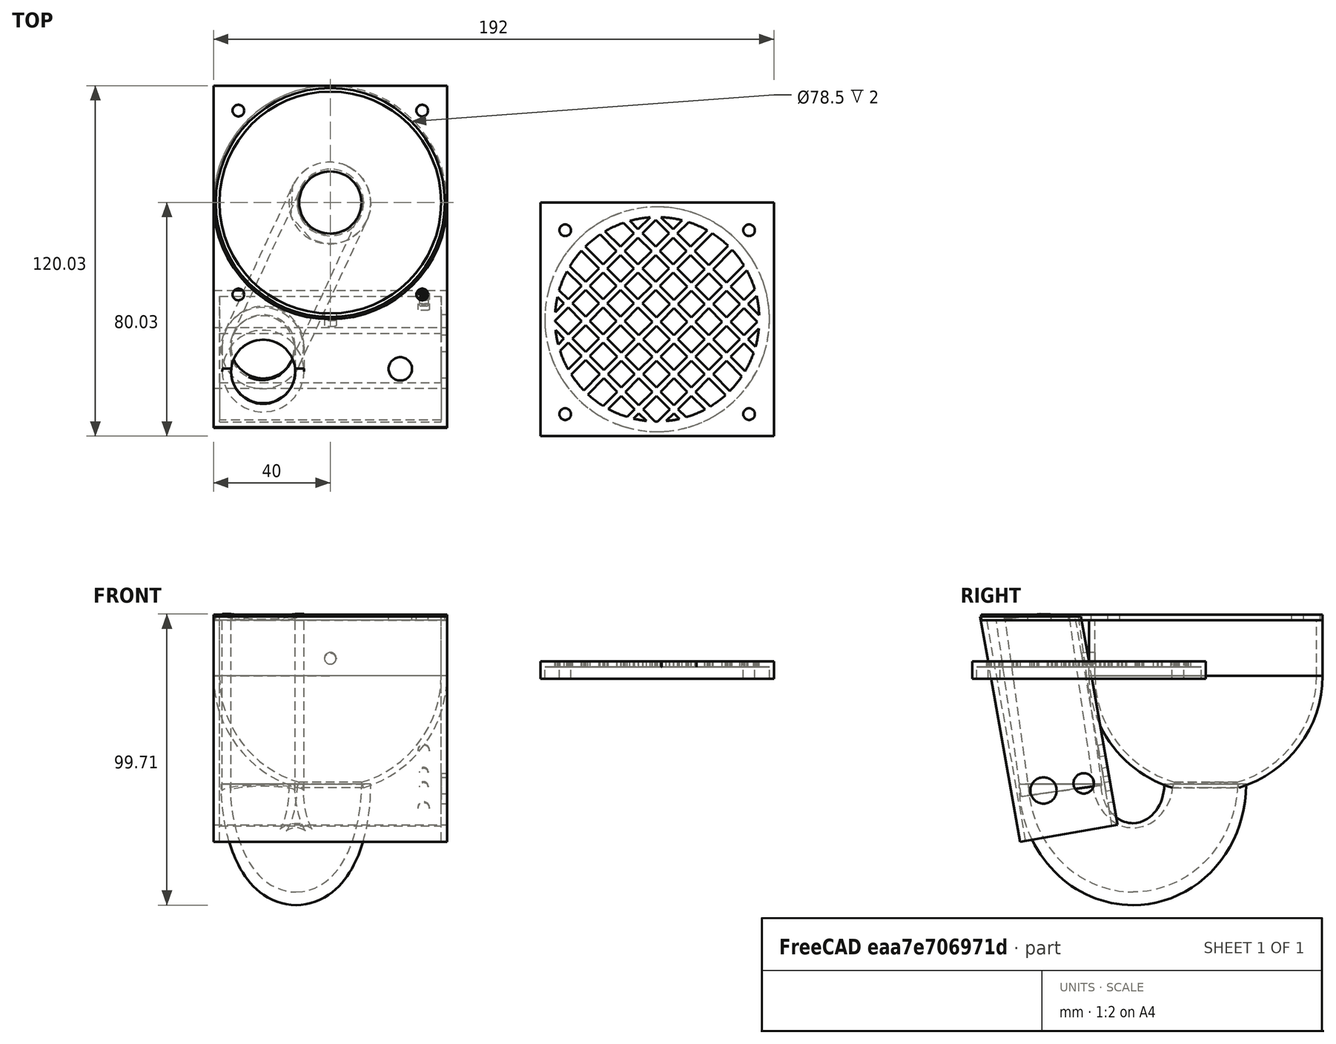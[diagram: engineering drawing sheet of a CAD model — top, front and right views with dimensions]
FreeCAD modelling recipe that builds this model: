
FCSTD DOCUMENT  (FreeCAD 0.18R16146 (Git))
Label: 10W75mmCabinet
License: All rights reserved
LicenseURL: http://en.wikipedia.org/wiki/All_rights_reserved
objects: Part::Cylinder×27, Part::Box×21, Part::MultiFuse×10, Part::Cut×7, Part::Sphere×3, Sketcher::SketchObject×2, Part::Sweep×2, Part::Spiral×1, PartDesign::Body×1
note: 74 computed .brp shape members not serialized (recipe doc carries the construction recipe); baked Part::Feature solids carry a one-line shape summary decoded from their .brp

FEATURE [Part::Sphere] Sphere  label="DomePunch"
  Angle1 = -90
  Angle2 = 90
  Angle3 = 360
  AttacherType = Attacher::AttachEngine3D
  Placement = pos=(38,38,0) rot=(0,0,1;0rad)
  Radius = 38
FEATURE [Part::Sphere] Sphere001  label="Dome"
  Angle1 = -90
  Angle2 = 90
  Angle3 = 360
  AttacherType = Attacher::AttachEngine3D
  Placement = pos=(38,38,0) rot=(0,0,1;0rad)
  Radius = 40
FEATURE [Part::Box] Box001  label="DomeSlice"
  AttacherType = Attacher::AttachEngine3D
  Height = 40
  Length = 80
  Placement = pos=(-2,-2,0) rot=(0,0,1;0rad)
  Width = 80
FEATURE [Part::Cylinder] Cylinder  label="DepthPunch"
  Angle = 360
  AttacherType = Attacher::AttachEngine3D
  Height = 20
  Placement = pos=(38,38,-1) rot=(0,0,1;0rad)
  Radius = 38
FEATURE [Part::Cylinder] Cylinder001  label="Depth"
  Angle = 360
  AttacherType = Attacher::AttachEngine3D
  Height = 19
  Placement = pos=(38,38,-1) rot=(0,0,1;0rad)
  Radius = 40
FEATURE [Part::Box] Box002  label="Mount"
  AttacherType = Attacher::AttachEngine3D
  Height = 2
  Length = 80
  Placement = pos=(-2,-39,20) rot=(0,0,1;0rad)
  Width = 117
FEATURE [Part::Cylinder] Cylinder002  label="MountPunch"
  Angle = 360
  AttacherType = Attacher::AttachEngine3D
  Height = 2
  Placement = pos=(38,38,20) rot=(0,0,1;0rad)
  Radius = 39.25
FEATURE [Part::Cylinder] Cylinder003  label="MountHole"
  Angle = 360
  AttacherType = Attacher::AttachEngine3D
  Height = 2
  Placement = pos=(0,0,20) rot=(0,0,1;0rad)
  Radius = 2
FEATURE [Part::Cylinder] Cylinder004  label="MountHole001"
  Angle = 360
  AttacherType = Attacher::AttachEngine3D
  Height = 2
  Placement = pos=(63,0,20) rot=(0,0,1;0rad)
  Radius = 2
FEATURE [Part::Cylinder] Cylinder005  label="MountHole002"
  Angle = 360
  AttacherType = Attacher::AttachEngine3D
  Height = 2
  Placement = pos=(63,63,20) rot=(0,0,1;0rad)
  Radius = 2
FEATURE [Part::Cylinder] Cylinder006  label="MountHole003"
  Angle = 360
  AttacherType = Attacher::AttachEngine3D
  Height = 2
  Placement = pos=(0,63,20) rot=(0,0,1;0rad)
  Radius = 2
FEATURE [Part::MultiFuse] Fusion  label="MountHoles"
  Placement = pos=(6.5,6.5,0) rot=(0,0,1;0rad)
  Shapes = -> [Cylinder003,Cylinder005,Cylinder006,Cylinder004]
FEATURE [Part::Box] Box003  label="Base"
  AttacherType = Attacher::AttachEngine3D
  Height = 80
  Length = 80
  Placement = pos=(-2,-33,-51) rot=(0,0,1;0rad)
  Width = 34
FEATURE [Part::Box] Box004  label="BasePunch"
  AttacherType = Attacher::AttachEngine3D
  Height = 78
  Length = 76
  Placement = pos=(0,-31,-51) rot=(0,0,1;0rad)
  Width = 30
FEATURE [Part::Cylinder] Cylinder007  label="BaseHole"
  Angle = 360
  AttacherType = Attacher::AttachEngine3D
  Height = 2
  Placement = pos=(15,-19,20) rot=(0,0,1;0rad)
  Radius = 11
FEATURE [Part::Sphere] Sphere002  label="DomeHole"
  Angle1 = -90
  Angle2 = 90
  Angle3 = 360
  AttacherType = Attacher::AttachEngine3D
  Placement = pos=(38,38,-42) rot=(0,0,1;0rad)
  Radius = 12
FEATURE [Part::MultiFuse] Fusion003  label="DOMEPUNCH"
  Shapes = -> [Sphere002,Sphere,Box001]
FEATURE [Part::Cut] Cut  label="DOME"
  Base = -> Sphere001
  Placement = pos=(0,2,1) rot=(0,0,1;0rad)
  Tool = -> Fusion003
FEATURE [Part::Cylinder] Cylinder008  label="Tube"
  Angle = 360
  AttacherType = Attacher::AttachEngine3D
  Height = 61
  Placement = pos=(15,-20,-39) rot=(0,0,1;0rad)
  Radius = 14
FEATURE [Part::Cylinder] Cylinder009  label="TubePunch"
  Angle = 360
  AttacherType = Attacher::AttachEngine3D
  Height = 61
  Placement = pos=(15,-20,-39) rot=(0,0,1;0rad)
  Radius = 11
FEATURE [Part::Spiral] Spiral001  label="TubeSpiral"
  AttacherType = Attacher::AttachEngine3D
  Growth = 1
  Placement = pos=(-2e-16,23,-70) rot=(0,0,1;1.5708rad)
  Radius = 27
  Rotations = 0.5
FEATURE [Part::Cylinder] Cylinder010  label="WireHole"
  Angle = 360
  AttacherType = Attacher::AttachEngine3D
  Height = 3
  Placement = pos=(38,1,5) rot=(1,0,0;1.5708rad)
  Radius = 2
FEATURE [Part::MultiFuse] Fusion004  label="DEPTHPUNCH"
  Shapes = -> [Cylinder,Cylinder010]
FEATURE [Part::Cut] Cut007  label="DEPTH"
  Base = -> Cylinder001
  Placement = pos=(0,2,2) rot=(0,0,1;0rad)
  Tool = -> Fusion004
FEATURE [Part::Cylinder] Cylinder012  label="VolumeHole"
  Angle = 360
  AttacherType = Attacher::AttachEngine3D
  Height = 2
  Placement = pos=(62,-20,20) rot=(0,0,1;0rad)
  Radius = 2.5
FEATURE [Part::Cylinder] Cylinder013  label="ExtSpeakerHole"
  Angle = 360
  AttacherType = Attacher::AttachEngine3D
  Height = 2
  Placement = pos=(70,1,-45) rot=(1,0,0;1.5708rad)
  Radius = 2
FEATURE [Part::Cylinder] Cylinder014  label="AudioInHole"
  Angle = 360
  AttacherType = Attacher::AttachEngine3D
  Height = 2
  Placement = pos=(76,-8,-35) rot=(0,1,0;1.5708rad)
  Radius = 3.5
FEATURE [Part::Cylinder] Cylinder015  label="PowerInHole"
  Angle = 360
  AttacherType = Attacher::AttachEngine3D
  Height = 2
  Placement = pos=(76,-22,-35) rot=(0,1,0;1.5708rad)
  Radius = 4.5
FEATURE [Sketcher::SketchObject] Sketch001  label="TubeSketchOuter"
  MapMode = 5
  Placement = pos=(0,0,0) rot=(0.57735,0.57735,0.57735;2.0944rad)
  Support = -> [YZ_Plane]
  sketch-geometry (1):
    g0: Circle CenterX=50.1616 CenterY=-70.1288 CenterZ=0 NormalX=0 NormalY=0 NormalZ=1 AngleXU=0 Radius=14.0264
FEATURE [Part::Sweep] Sweep
  Frenet = false
  Placement = pos=(-45.2015,16.8804,-37.1345) rot=(-0.179283,-0.967324,-0.179283;1.60401rad)
  Sections = -> [Sketch001]
  Solid = true
  Spine = -> Spiral001 [Edge1]
  Transition = 1
FEATURE [Sketcher::SketchObject] Sketch  label="SketchInner"
  MapMode = 5
  Placement = pos=(0,0,0) rot=(0.57735,0.57735,0.57735;2.0944rad)
  Support = -> [YZ_Plane]
  sketch-geometry (1):
    g0: Circle CenterX=50.2486 CenterY=-70.2529 CenterZ=0 NormalX=0 NormalY=0 NormalZ=1 AngleXU=0 Radius=11.0039
FEATURE [PartDesign::Body] Body  label="TubeBodyOuter"
  Group = -> [Sketch001,Sketch]
  Origin = -> Origin
FEATURE [Part::Sweep] Sweep001
  Frenet = false
  Placement = pos=(-45.3803,16.9935,-35.5882) rot=(-0.179283,-0.967324,-0.179283;1.60401rad)
  Sections = -> [Sketch]
  Solid = true
  Spine = -> Spiral001 [Edge1]
  Transition = 1
FEATURE [Part::Cut] Cut008  label="TUBE_CURVE"
  Base = -> Sweep
  Placement = pos=(-3,4,1) rot=(0,0,-1;0.069813rad)
  Tool = -> Sweep001
FEATURE [Part::Cylinder] Cylinder016  label="FaceHole"
  Angle = 360
  AttacherType = Attacher::AttachEngine3D
  Height = 4
  Placement = pos=(150,0,0) rot=(0,0,1;0rad)
  Radius = 38.5
FEATURE [Part::Box] Box  label="Face"
  AttacherType = Attacher::AttachEngine3D
  Height = 6
  Length = 80
  Placement = pos=(110,-40,0) rot=(0,0,1;0rad)
  Width = 80
FEATURE [Part::Cylinder] Cylinder017  label="FaceSpace"
  Angle = 360
  AttacherType = Attacher::AttachEngine3D
  Height = 2
  Placement = pos=(150,0,4) rot=(0,0,1;0rad)
  Radius = 35
FEATURE [Part::Cylinder] Cylinder018  label="MountHole004"
  Angle = 360
  AttacherType = Attacher::AttachEngine3D
  Height = 6
  Placement = pos=(0,0,20) rot=(0,0,1;0rad)
  Radius = 2
FEATURE [Part::Cylinder] Cylinder019  label="MountHole005"
  Angle = 360
  AttacherType = Attacher::AttachEngine3D
  Height = 6
  Placement = pos=(63,0,20) rot=(0,0,1;0rad)
  Radius = 2
FEATURE [Part::Cylinder] Cylinder020  label="MountHole006"
  Angle = 360
  AttacherType = Attacher::AttachEngine3D
  Height = 6
  Placement = pos=(63,63,20) rot=(0,0,1;0rad)
  Radius = 2
FEATURE [Part::Cylinder] Cylinder021  label="MountHole007"
  Angle = 360
  AttacherType = Attacher::AttachEngine3D
  Height = 6
  Placement = pos=(0,63,20) rot=(0,0,1;0rad)
  Radius = 2
FEATURE [Part::MultiFuse] Fusion006  label="FaceMountHoles"
  Placement = pos=(118.5,-32.5,-20) rot=(0,0,1;0rad)
  Shapes = -> [Cylinder018,Cylinder020,Cylinder021,Cylinder019]
FEATURE [Part::MultiFuse] Fusion005  label="FacePunch"
  Shapes = -> [Cylinder017,Cylinder016,Fusion006]
FEATURE [Part::Box] Box005  label="Grill"
  AttacherType = Attacher::AttachEngine3D
  Height = 2
  Length = 75
  Placement = pos=(124.5,-27.5,4) rot=(0,0,1;0.785398rad)
  Width = 2
FEATURE [Part::Box] Box006  label="Grill001"
  AttacherType = Attacher::AttachEngine3D
  Height = 2
  Length = 75
  Placement = pos=(122.5,25,4) rot=(0,0,-1;0.785398rad)
  Width = 2
FEATURE [Part::Box] Box007  label="Grill002"
  AttacherType = Attacher::AttachEngine3D
  Height = 2
  Length = 75
  Placement = pos=(118,-21.5,4) rot=(0,0,1;0.785398rad)
  Width = 2
FEATURE [Part::Box] Box008  label="Grill003"
  AttacherType = Attacher::AttachEngine3D
  Height = 2
  Length = 58
  Placement = pos=(112,-3.5,4) rot=(0,0,1;0.785398rad)
  Width = 2
FEATURE [Part::Box] Box009  label="Grill004"
  AttacherType = Attacher::AttachEngine3D
  Height = 2
  Length = 75
  Placement = pos=(112,-15.5,4) rot=(0,0,1;0.785398rad)
  Width = 2
FEATURE [Part::Box] Box010  label="Grill005"
  AttacherType = Attacher::AttachEngine3D
  Height = 2
  Length = 75
  Placement = pos=(128.5,31,4) rot=(0,0,-1;0.785398rad)
  Width = 2
FEATURE [Part::Box] Box011  label="Grill006"
  AttacherType = Attacher::AttachEngine3D
  Height = 2
  Length = 75
  Placement = pos=(134.5,37,4) rot=(0,0,-1;0.785398rad)
  Width = 2
FEATURE [Part::Box] Box012  label="Grill007"
  AttacherType = Attacher::AttachEngine3D
  Height = 2
  Length = 58
  Placement = pos=(146.5,37,4) rot=(0,0,-1;0.785398rad)
  Width = 2
FEATURE [Part::Box] Box013  label="Grill008"
  AttacherType = Attacher::AttachEngine3D
  Height = 2
  Length = 75
  Placement = pos=(116.5,19,4) rot=(0,0,-1;0.785398rad)
  Width = 2
FEATURE [Part::Box] Box014  label="Grill009"
  AttacherType = Attacher::AttachEngine3D
  Height = 2
  Length = 75
  Placement = pos=(110.5,13,4) rot=(0,0,-1;0.785398rad)
  Width = 2
FEATURE [Part::Box] Box015  label="Grill010"
  AttacherType = Attacher::AttachEngine3D
  Height = 2
  Length = 58
  Placement = pos=(110.5,1,4) rot=(0,0,-1;0.785398rad)
  Width = 2
FEATURE [Part::Box] Box016  label="Grill011"
  AttacherType = Attacher::AttachEngine3D
  Height = 2
  Length = 75
  Placement = pos=(130.5,-33.5,4) rot=(0,0,1;0.785398rad)
  Width = 2
FEATURE [Part::Box] Box017  label="Grill012"
  AttacherType = Attacher::AttachEngine3D
  Height = 2
  Length = 75
  Placement = pos=(136.5,-39.5,4) rot=(0,0,1;0.785398rad)
  Width = 2
FEATURE [Part::Box] Box018  label="Grill013"
  AttacherType = Attacher::AttachEngine3D
  Height = 2
  Length = 58
  Placement = pos=(148.5,-39.5,4) rot=(0,0,1;0.785398rad)
  Width = 2
FEATURE [Part::MultiFuse] Fusion007  label="GRILL"
  Shapes = -> [Box005,Box006,Box007,Box008,Box009,Box010,Box011,Box012,Box013,Box014,Box015,Box016,Box017,Box018]
FEATURE [Part::Cut] Cut009  label="FACE"
  Base = -> Box
  Tool = -> Fusion005
FEATURE [Part::Box] Box019  label="FrontLevel"
  AttacherType = Attacher::AttachEngine3D
  Height = 8
  Length = 80
  Placement = pos=(-2,-36,28) rot=(-1,0,0;0.174533rad)
  Width = 38
FEATURE [Part::Cylinder] Cylinder022  label="MountTubeHole"
  Angle = 360
  AttacherType = Attacher::AttachEngine3D
  Height = 2
  Placement = pos=(15,-20,20) rot=(0,0,1;0rad)
  Radius = 11
FEATURE [Part::Cylinder] Cylinder023  label="VolumeHole001"
  Angle = 360
  AttacherType = Attacher::AttachEngine3D
  Height = 2
  Placement = pos=(62,-19,20) rot=(0,0,1;0rad)
  Radius = 4
FEATURE [Part::MultiFuse] Fusion001  label="MOUNTPUNCH"
  Shapes = -> [Cylinder002,Fusion,Cylinder022,Cylinder023]
FEATURE [Part::Cut] Cut013  label="MOUNT"
  Base = -> Box002
  Placement = pos=(0,2,0) rot=(0,0,1;0rad)
  Tool = -> Fusion001
FEATURE [Part::Cylinder] Cylinder024  label="WireHole002"
  Angle = 360
  AttacherType = Attacher::AttachEngine3D
  Height = 3
  Placement = pos=(38,1,7) rot=(1,0,0;1.5708rad)
  Radius = 2
FEATURE [Part::Cylinder] Cylinder025  label="ExtSpeakerHole001"
  Angle = 360
  AttacherType = Attacher::AttachEngine3D
  Height = 2
  Placement = pos=(70,1,-25) rot=(1,0,0;1.5708rad)
  Radius = 2
FEATURE [Part::Cylinder] Cylinder026  label="ExtSpeakerHole002"
  Angle = 360
  AttacherType = Attacher::AttachEngine3D
  Height = 2
  Placement = pos=(70,1,-32.5) rot=(1,0,0;1.5708rad)
  Radius = 1.5
FEATURE [Part::Cylinder] Cylinder027  label="ExtSpeakerHole003"
  Angle = 360
  AttacherType = Attacher::AttachEngine3D
  Height = 2
  Placement = pos=(70,1,-37.5) rot=(1,0,0;1.5708rad)
  Radius = 1.5
FEATURE [Part::MultiFuse] Fusion008  label="BASEPUNCH"
  Shapes = -> [Box004,Cylinder007,Cylinder012,Cylinder013,Cylinder014,Cylinder015,Box019,Cylinder024,Cylinder025,Cylinder026,Cylinder027]
FEATURE [Part::Cut] Cut012  label="BASE"
  Base = -> Box003
  Placement = pos=(0,0,0) rot=(1,0,0;0.174533rad)
  Tool = -> Fusion008
FEATURE [Part::MultiFuse] Fusion009  label="FACEGRILL"
  Shapes = -> [Fusion007,Cut009]
FEATURE [Part::Box] Box020  label="FrontLevel001"
  AttacherType = Attacher::AttachEngine3D
  Height = 8
  Length = 32
  Placement = pos=(-2,-36,25) rot=(-1,0,0;0.174533rad)
  Width = 32
FEATURE [Part::MultiFuse] Fusion010  label="TUBEPUNCH"
  Shapes = -> [Box020,Cylinder009]
FEATURE [Part::Cut] Cut014  label="TUBE"
  Base = -> Cylinder008
  Placement = pos=(0,5,3) rot=(1,0,0;0.139626rad)
  Tool = -> Fusion010
